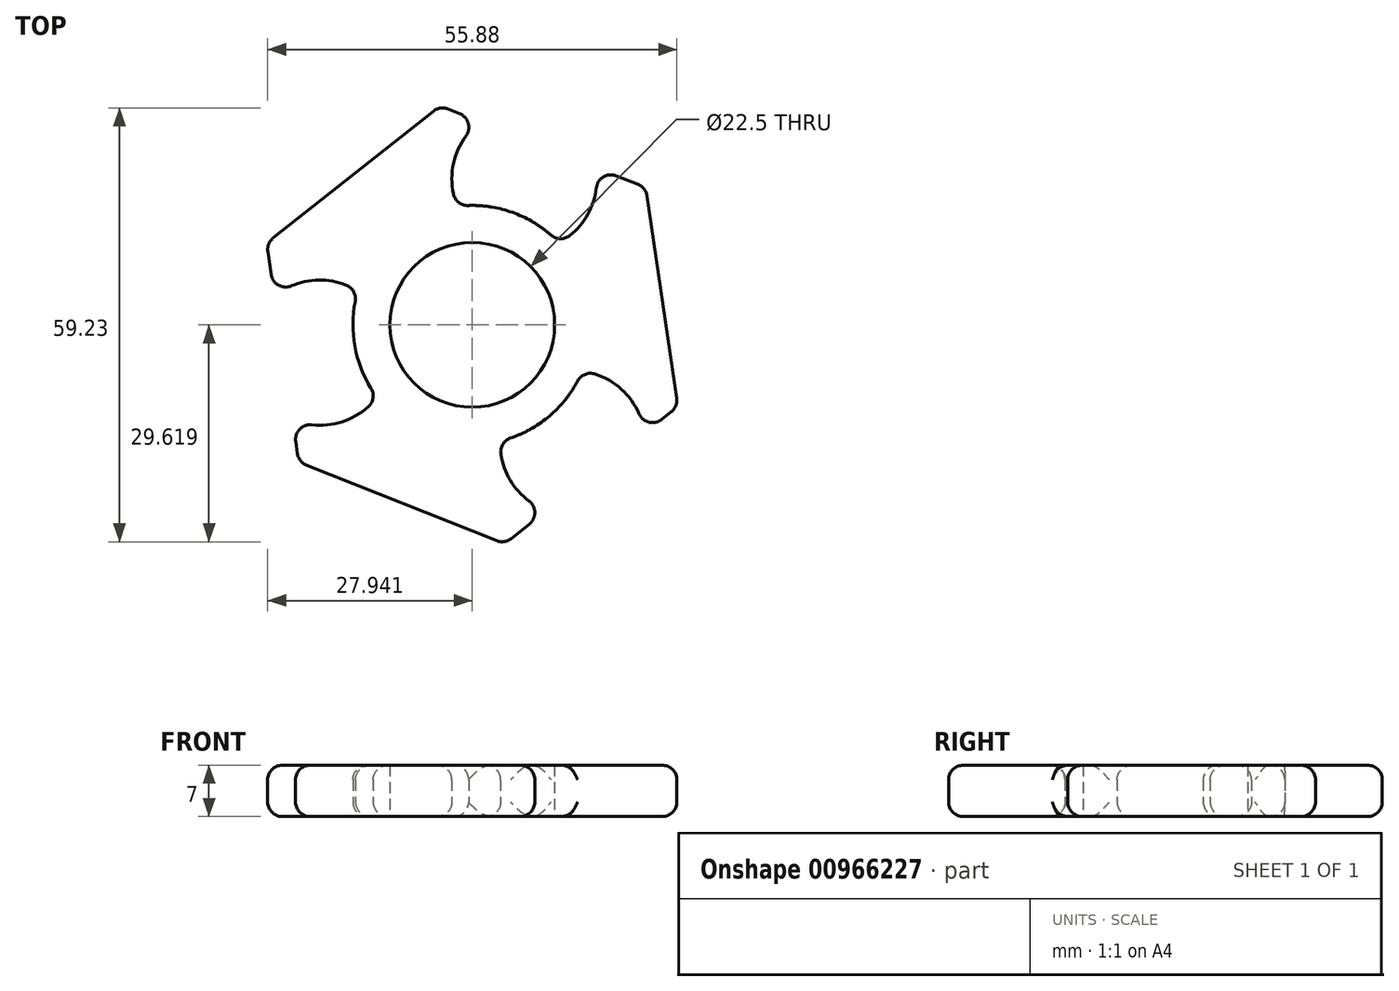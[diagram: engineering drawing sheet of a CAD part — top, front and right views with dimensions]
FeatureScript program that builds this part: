
annotation { "Feature Type Name" : "Feature", "Feature Type Description" : "" }
export const myFeature = defineFeature(function(context is Context, id is Id, definition is map)
    precondition{}
    {
        {
            var Q0;
            Q0=qCreatedBy(makeId("Top.planeOp"),FACE);
            var sketch = newSketch(context, id + "F0", { "sketchPlane" : qUnion([Q0])});
            skCircle(sketch, "E0", {"center": v(-239.75, -46.72) * mm, "radius": 11.25 * mm});
            skCircle(sketch, "E1.cCircle", {"center": v(-239.75, -46.72) * mm, "radius": 26.17 * mm, "construction": true});
            skLineSegment(sketch, "E1.0", {"start": v(-216.05, -27.97) * mm, "end": v(-211.66, -57.87) * mm});
            skLineSegment(sketch, "E1.1", {"start": v(-211.66, -57.87) * mm, "end": v(-235.36, -76.62) * mm});
            skLineSegment(sketch, "E1.2", {"start": v(-235.36, -76.62) * mm, "end": v(-263.45, -65.47) * mm});
            skLineSegment(sketch, "E1.3", {"start": v(-263.45, -65.47) * mm, "end": v(-267.84, -35.57) * mm});
            skLineSegment(sketch, "E1.4", {"start": v(-267.84, -35.57) * mm, "end": v(-244.14, -16.82) * mm});
            skLineSegment(sketch, "E1.5", {"start": v(-244.14, -16.82) * mm, "end": v(-216.05, -27.97) * mm});
            skPoint(sketch, "E1.0.midPoint", {"position": v(-213.85, -42.92) * mm});
            skCircle(sketch, "E2", {"center": v(-260.57, -50.52) * mm, "radius": 9.91 * mm});
            skPoint(sketch, "E2.centerSnap0", {"position": v(-265.64, -50.52) * mm});
            skCircle(sketch, "E3.1.0", {"center": v(-226.05, -62.85) * mm, "radius": 9.91 * mm});
            skCircle(sketch, "E3.2.0", {"center": v(-232.63, -26.8) * mm, "radius": 9.91 * mm});
            skCircle(sketch, "E4", {"center": v(-239.75, -46.72) * mm, "radius": 16.3 * mm});
            skSolve(sketch);
        }
        {
            var Q0;
            {var subQ1=sQuery(id+"F0.wireOp",EDGE,"E1.0");Q0=makeQuery(id+"F0.imprint","IMPRINT",FACE,{"disambiguationData":[TD([[makeQuery(id+"F0.imprint","IMPRINT",EDGE,{"derivedFrom":subQ1}),-1.0]])]});}
            var Q1;
            {var subQ1=sQuery(id+"F0.wireOp",EDGE,"E1.4");Q1=makeQuery(id+"F0.imprint","IMPRINT",FACE,{"disambiguationData":[TD([[makeQuery(id+"F0.imprint","IMPRINT",EDGE,{"derivedFrom":subQ1}),-1.0]])]});}
            var Q2;
            {var subQ1=sQuery(id+"F0.wireOp",EDGE,"E1.2");Q2=makeQuery(id+"F0.imprint","IMPRINT",FACE,{"disambiguationData":[TD([[makeQuery(id+"F0.imprint","IMPRINT",EDGE,{"derivedFrom":subQ1}),-1.0]])]});}
            var Q3;
            {var subQ0=sQuery(id+"F0.wireOp",EDGE,"E2");var subQ1=sQuery(id+"F0.wireOp",EDGE,"E0");var subQ2=makeQuery(id+"F0.imprint","INTERSECT",VERTEX,{"derivedFrom":[subQ1,subQ0]});Q3=makeQuery(id+"F0.imprint","IMPRINT",FACE,{"disambiguationData":[TD([[makeQuery(id+"F0.imprint","IMPRINT",EDGE,{"disambiguationData":[TD([[subQ2,1.0]])],"derivedFrom":subQ1}),-1.0]])]});}
            var Q4;
            {var subQ0=sQuery(id+"F0.wireOp",EDGE,"E2");var subQ1=makeQuery(id+"F0.imprint","INTERSECT",VERTEX,{"derivedFrom":[sQuery(id+"F0.wireOp",EDGE,"E0"),subQ0]});Q4=makeQuery(id+"F0.imprint","IMPRINT",FACE,{"disambiguationData":[TD([[makeQuery(id+"F0.imprint","IMPRINT",EDGE,{"disambiguationData":[TD([[subQ1,-1.0]])],"derivedFrom":subQ0}),1.0]])]});}
            var Q5;
            {var subQ0=sQuery(id+"F0.wireOp",EDGE,"E2");var subQ1=sQuery(id+"F0.wireOp",EDGE,"E0");var subQ2=makeQuery(id+"F0.imprint","INTERSECT",VERTEX,{"derivedFrom":[subQ1,subQ0]});Q5=makeQuery(id+"F0.imprint","IMPRINT",FACE,{"disambiguationData":[TD([[makeQuery(id+"F0.imprint","IMPRINT",EDGE,{"disambiguationData":[TD([[subQ2,-1.0]])],"derivedFrom":subQ1}),-1.0]])]});}
            var Q6;
            {var subQ0=sQuery(id+"F0.wireOp",EDGE,"E3.1.0");var subQ1=makeQuery(id+"F0.imprint","INTERSECT",VERTEX,{"derivedFrom":[sQuery(id+"F0.wireOp",EDGE,"E0"),subQ0]});Q6=makeQuery(id+"F0.imprint","IMPRINT",FACE,{"disambiguationData":[TD([[makeQuery(id+"F0.imprint","IMPRINT",EDGE,{"disambiguationData":[TD([[subQ1,-1.0]])],"derivedFrom":subQ0}),1.0]])]});}
            var Q7;
            {var subQ0=sQuery(id+"F0.wireOp",EDGE,"E3.2.0");var subQ1=sQuery(id+"F0.wireOp",EDGE,"E0");var subQ2=makeQuery(id+"F0.imprint","INTERSECT",VERTEX,{"derivedFrom":[subQ1,subQ0]});Q7=makeQuery(id+"F0.imprint","IMPRINT",FACE,{"disambiguationData":[TD([[makeQuery(id+"F0.imprint","IMPRINT",EDGE,{"disambiguationData":[TD([[subQ2,1.0]])],"derivedFrom":subQ1}),-1.0]])]});}
            var Q8;
            {var subQ0=sQuery(id+"F0.wireOp",EDGE,"E3.2.0");var subQ1=makeQuery(id+"F0.imprint","INTERSECT",VERTEX,{"derivedFrom":[sQuery(id+"F0.wireOp",EDGE,"E0"),subQ0]});Q8=makeQuery(id+"F0.imprint","IMPRINT",FACE,{"disambiguationData":[TD([[makeQuery(id+"F0.imprint","IMPRINT",EDGE,{"disambiguationData":[TD([[subQ1,-1.0]])],"derivedFrom":subQ0}),1.0]])]});}
            extrude(context, id + "F1", {"entities" : qUnion([Q0, Q1, Q2, Q3, Q4, Q5, Q6, Q7, Q8]), "depth" : 7 * mm, "offsetDistance" : 25 * mm});
        }
        {
            var Q0;
            Q0=makeQuery(id+"F1.opExtrude","CAP_EDGE",EDGE,{"disambiguationData":[OSD([sQuery(id+"F0.wireOp",EDGE,"E1.4")])],"isStart":false});
            var Q1;
            Q1=makeQuery(id+"F1.opExtrude","CAP_EDGE",EDGE,{"disambiguationData":[OSD([sQuery(id+"F0.wireOp",EDGE,"E1.0")])],"isStart":false});
            var Q2;
            Q2=makeQuery(id+"F1.opExtrude","CAP_EDGE",EDGE,{"disambiguationData":[OSD([sQuery(id+"F0.wireOp",EDGE,"E1.2")])],"isStart":false});
            var Q3;
            {var subQ0=sQuery(id+"F0.wireOp",EDGE,"E1.3");Q3=makeQuery(id+"F1.opExtrude","CAP_EDGE",EDGE,{"disambiguationData":[OSD([subQ0]),TDD([makeQuery(id+"F0.imprint","IMPRINT",EDGE,{"disambiguationData":[TD([[makeQuery(id+"F0.imprint","INTERSECT",VERTEX,{"derivedFrom":[subQ0,sQuery(id+"F0.wireOp",EDGE,"E1.4")]}),1.0]])],"derivedFrom":subQ0})])],"isStart":false});}
            var Q4;
            {var subQ0=sQuery(id+"F0.wireOp",EDGE,"E1.3");Q4=makeQuery(id+"F1.opExtrude","CAP_EDGE",EDGE,{"disambiguationData":[OSD([subQ0]),TDD([makeQuery(id+"F0.imprint","IMPRINT",EDGE,{"disambiguationData":[TD([[makeQuery(id+"F0.imprint","INTERSECT",VERTEX,{"derivedFrom":[sQuery(id+"F0.wireOp",EDGE,"E1.2"),subQ0]}),-1.0]])],"derivedFrom":subQ0})])],"isStart":false});}
            var Q5;
            {var subQ0=sQuery(id+"F0.wireOp",EDGE,"E4");var subQ1=sQuery(id+"F0.wireOp",EDGE,"E2");Q5=makeQuery(id+"F1.opExtrude","CAP_EDGE",EDGE,{"disambiguationData":[OSD([subQ0]),TDD([makeQuery(id+"F0.imprint","IMPRINT",EDGE,{"disambiguationData":[TD([[makeQuery(id+"F0.imprint","INTERSECT",VERTEX,{"disambiguationData":[OD(0.0)],"derivedFrom":[subQ1,subQ0]}),-1.0]])],"derivedFrom":subQ0})])],"isStart":false});}
            var Q6;
            {var subQ0=sQuery(id+"F0.wireOp",EDGE,"E2");Q6=makeQuery(id+"F1.opExtrude","CAP_EDGE",EDGE,{"disambiguationData":[OSD([subQ0]),TDD([makeQuery(id+"F0.imprint","IMPRINT",EDGE,{"disambiguationData":[TD([[makeQuery(id+"F0.imprint","INTERSECT",VERTEX,{"disambiguationData":[OD(1.0)],"derivedFrom":[sQuery(id+"F0.wireOp",EDGE,"E1.3"),subQ0]}),1.0]])],"derivedFrom":subQ0})])],"isStart":false});}
            var Q7;
            {var subQ0=sQuery(id+"F0.wireOp",EDGE,"E2");Q7=makeQuery(id+"F1.opExtrude","CAP_EDGE",EDGE,{"disambiguationData":[OSD([subQ0]),TDD([makeQuery(id+"F0.imprint","IMPRINT",EDGE,{"disambiguationData":[TD([[makeQuery(id+"F0.imprint","INTERSECT",VERTEX,{"disambiguationData":[OD(0.0)],"derivedFrom":[sQuery(id+"F0.wireOp",EDGE,"E1.3"),subQ0]}),-1.0]])],"derivedFrom":subQ0})])],"isStart":false});}
            var Q8;
            {var subQ0=sQuery(id+"F0.wireOp",EDGE,"E3.1.0");Q8=makeQuery(id+"F1.opExtrude","CAP_EDGE",EDGE,{"disambiguationData":[OSD([subQ0]),TDD([makeQuery(id+"F0.imprint","IMPRINT",EDGE,{"disambiguationData":[TD([[makeQuery(id+"F0.imprint","INTERSECT",VERTEX,{"disambiguationData":[OD(1.0)],"derivedFrom":[sQuery(id+"F0.wireOp",EDGE,"E1.1"),subQ0]}),1.0]])],"derivedFrom":subQ0})])],"isStart":false});}
            var Q9;
            {var subQ0=sQuery(id+"F0.wireOp",EDGE,"E4");var subQ1=sQuery(id+"F0.wireOp",EDGE,"E3.1.0");Q9=makeQuery(id+"F1.opExtrude","SWEPT_FACE",FACE,{"disambiguationData":[OSD([subQ0]),TDD([makeQuery(id+"F0.imprint","IMPRINT",EDGE,{"disambiguationData":[TD([[makeQuery(id+"F0.imprint","INTERSECT",VERTEX,{"disambiguationData":[OD(0.0)],"derivedFrom":[subQ1,subQ0]}),-1.0]])],"derivedFrom":subQ0})])]});}
            var Q10;
            {var subQ0=sQuery(id+"F0.wireOp",EDGE,"E2");Q10=makeQuery(id+"F1.opExtrude","CAP_EDGE",EDGE,{"disambiguationData":[OSD([subQ0]),TDD([makeQuery(id+"F0.imprint","IMPRINT",EDGE,{"disambiguationData":[TD([[makeQuery(id+"F0.imprint","INTERSECT",VERTEX,{"disambiguationData":[OD(1.0)],"derivedFrom":[sQuery(id+"F0.wireOp",EDGE,"E1.3"),subQ0]}),1.0]])],"derivedFrom":subQ0})])],"isStart":true});}
            var Q11;
            {var subQ0=sQuery(id+"F0.wireOp",EDGE,"E4");var subQ1=sQuery(id+"F0.wireOp",EDGE,"E3.2.0");Q11=makeQuery(id+"F1.opExtrude","CAP_EDGE",EDGE,{"disambiguationData":[OSD([subQ0]),TDD([makeQuery(id+"F0.imprint","IMPRINT",EDGE,{"disambiguationData":[TD([[makeQuery(id+"F0.imprint","INTERSECT",VERTEX,{"disambiguationData":[OD(0.0)],"derivedFrom":[subQ1,subQ0]}),-1.0]])],"derivedFrom":subQ0})])],"isStart":false});}
            var Q12;
            {var subQ0=sQuery(id+"F0.wireOp",EDGE,"E4");var subQ1=sQuery(id+"F0.wireOp",EDGE,"E3.2.0");Q12=makeQuery(id+"F1.opExtrude","CAP_EDGE",EDGE,{"disambiguationData":[OSD([subQ0]),TDD([makeQuery(id+"F0.imprint","IMPRINT",EDGE,{"disambiguationData":[TD([[makeQuery(id+"F0.imprint","INTERSECT",VERTEX,{"disambiguationData":[OD(0.0)],"derivedFrom":[subQ1,subQ0]}),-1.0]])],"derivedFrom":subQ0})])],"isStart":true});}
            var Q13;
            {var subQ0=sQuery(id+"F0.wireOp",EDGE,"E3.1.0");Q13=makeQuery(id+"F1.opExtrude","CAP_EDGE",EDGE,{"disambiguationData":[OSD([subQ0]),TDD([makeQuery(id+"F0.imprint","IMPRINT",EDGE,{"disambiguationData":[TD([[makeQuery(id+"F0.imprint","INTERSECT",VERTEX,{"disambiguationData":[OD(1.0)],"derivedFrom":[sQuery(id+"F0.wireOp",EDGE,"E1.1"),subQ0]}),1.0]])],"derivedFrom":subQ0})])],"isStart":true});}
            var Q14;
            Q14=makeQuery(id+"F1.opExtrude","SWEPT_EDGE",EDGE,{"disambiguationData":[OSD([sQuery(id+"F0.wireOp",EDGE,"E1.4"),sQuery(id+"F0.wireOp",EDGE,"E1.5")])]});
            var Q15;
            Q15=makeQuery(id+"F1.opExtrude","SWEPT_EDGE",EDGE,{"disambiguationData":[OSD([sQuery(id+"F0.wireOp",EDGE,"E1.0"),sQuery(id+"F0.wireOp",EDGE,"E1.5")])]});
            var Q16;
            {var subQ0=sQuery(id+"F0.wireOp",EDGE,"E3.1.0");Q16=makeQuery(id+"F1.opExtrude","CAP_EDGE",EDGE,{"disambiguationData":[OSD([subQ0]),TDD([makeQuery(id+"F0.imprint","IMPRINT",EDGE,{"disambiguationData":[TD([[makeQuery(id+"F0.imprint","INTERSECT",VERTEX,{"disambiguationData":[OD(0.0)],"derivedFrom":[sQuery(id+"F0.wireOp",EDGE,"E1.1"),subQ0]}),-1.0]])],"derivedFrom":subQ0})])],"isStart":true});}
            var Q17;
            {var subQ0=sQuery(id+"F0.wireOp",EDGE,"E1.1");Q17=makeQuery(id+"F1.opExtrude","CAP_EDGE",EDGE,{"disambiguationData":[OSD([subQ0]),TDD([makeQuery(id+"F0.imprint","IMPRINT",EDGE,{"disambiguationData":[TD([[makeQuery(id+"F0.imprint","INTERSECT",VERTEX,{"derivedFrom":[sQuery(id+"F0.wireOp",EDGE,"E1.0"),subQ0]}),-1.0]])],"derivedFrom":subQ0})])],"isStart":true});}
            var Q18;
            {var subQ0=sQuery(id+"F0.wireOp",EDGE,"E4");var subQ1=sQuery(id+"F0.wireOp",EDGE,"E2");Q18=makeQuery(id+"F1.opExtrude","CAP_EDGE",EDGE,{"disambiguationData":[OSD([subQ0]),TDD([makeQuery(id+"F0.imprint","IMPRINT",EDGE,{"disambiguationData":[TD([[makeQuery(id+"F0.imprint","INTERSECT",VERTEX,{"disambiguationData":[OD(0.0)],"derivedFrom":[subQ1,subQ0]}),-1.0]])],"derivedFrom":subQ0})])],"isStart":true});}
            var Q19;
            {var subQ0=sQuery(id+"F0.wireOp",EDGE,"E4");var subQ1=sQuery(id+"F0.wireOp",EDGE,"E3.1.0");Q19=makeQuery(id+"F1.opExtrude","CAP_EDGE",EDGE,{"disambiguationData":[OSD([subQ0]),TDD([makeQuery(id+"F0.imprint","IMPRINT",EDGE,{"disambiguationData":[TD([[makeQuery(id+"F0.imprint","INTERSECT",VERTEX,{"disambiguationData":[OD(0.0)],"derivedFrom":[subQ1,subQ0]}),-1.0]])],"derivedFrom":subQ0})])],"isStart":true});}
            var Q20;
            Q20=makeQuery(id+"F1.opExtrude","SWEPT_EDGE",EDGE,{"disambiguationData":[OSD([sQuery(id+"F0.wireOp",EDGE,"E1.0"),sQuery(id+"F0.wireOp",EDGE,"E1.1")])]});
            var Q21;
            Q21=makeQuery(id+"F1.opExtrude","SWEPT_EDGE",EDGE,{"disambiguationData":[OSD([sQuery(id+"F0.wireOp",EDGE,"E1.3"),sQuery(id+"F0.wireOp",EDGE,"E1.4")])]});
            var Q22;
            Q22=makeQuery(id+"F1.opExtrude","SWEPT_EDGE",EDGE,{"disambiguationData":[OSD([sQuery(id+"F0.wireOp",EDGE,"E1.2"),sQuery(id+"F0.wireOp",EDGE,"E1.3")])]});
            var Q23;
            {var subQ0=sQuery(id+"F0.wireOp",EDGE,"E4");var subQ1=sQuery(id+"F0.wireOp",EDGE,"E2");Q23=makeQuery(id+"F1.opExtrude","SWEPT_EDGE",EDGE,{"disambiguationData":[OSD([subQ1,subQ0]),TDD([makeQuery(id+"F0.imprint","INTERSECT",VERTEX,{"disambiguationData":[OD(1.0)],"derivedFrom":[subQ1,subQ0]})])]});}
            var Q24;
            {var subQ0=sQuery(id+"F0.wireOp",EDGE,"E1.1");Q24=makeQuery(id+"F1.opExtrude","CAP_EDGE",EDGE,{"disambiguationData":[OSD([subQ0]),TDD([makeQuery(id+"F0.imprint","IMPRINT",EDGE,{"disambiguationData":[TD([[makeQuery(id+"F0.imprint","INTERSECT",VERTEX,{"derivedFrom":[sQuery(id+"F0.wireOp",EDGE,"E1.0"),subQ0]}),-1.0]])],"derivedFrom":subQ0})])],"isStart":false});}
            var Q25;
            Q25=makeQuery(id+"F1.opExtrude","CAP_EDGE",EDGE,{"disambiguationData":[OSD([sQuery(id+"F0.wireOp",EDGE,"E1.4")])],"isStart":true});
            var Q26;
            {var subQ0=sQuery(id+"F0.wireOp",EDGE,"E3.1.0");Q26=makeQuery(id+"F1.opExtrude","CAP_EDGE",EDGE,{"disambiguationData":[OSD([subQ0]),TDD([makeQuery(id+"F0.imprint","IMPRINT",EDGE,{"disambiguationData":[TD([[makeQuery(id+"F0.imprint","INTERSECT",VERTEX,{"disambiguationData":[OD(0.0)],"derivedFrom":[sQuery(id+"F0.wireOp",EDGE,"E1.1"),subQ0]}),-1.0]])],"derivedFrom":subQ0})])],"isStart":false});}
            var Q27;
            Q27=makeQuery(id+"F1.opExtrude","SWEPT_EDGE",EDGE,{"disambiguationData":[OSD([sQuery(id+"F0.wireOp",EDGE,"E1.1"),sQuery(id+"F0.wireOp",EDGE,"E1.2")])]});
            var Q28;
            {var subQ0=sQuery(id+"F0.wireOp",EDGE,"E4");var subQ1=sQuery(id+"F0.wireOp",EDGE,"E3.1.0");Q28=makeQuery(id+"F1.opExtrude","SWEPT_EDGE",EDGE,{"disambiguationData":[OSD([subQ1,subQ0]),TDD([makeQuery(id+"F0.imprint","INTERSECT",VERTEX,{"disambiguationData":[OD(1.0)],"derivedFrom":[subQ1,subQ0]})])]});}
            var Q29;
            {var subQ0=sQuery(id+"F0.wireOp",EDGE,"E1.3");Q29=makeQuery(id+"F1.opExtrude","CAP_EDGE",EDGE,{"disambiguationData":[OSD([subQ0]),TDD([makeQuery(id+"F0.imprint","IMPRINT",EDGE,{"disambiguationData":[TD([[makeQuery(id+"F0.imprint","INTERSECT",VERTEX,{"derivedFrom":[subQ0,sQuery(id+"F0.wireOp",EDGE,"E1.4")]}),1.0]])],"derivedFrom":subQ0})])],"isStart":true});}
            var Q30;
            {var subQ0=sQuery(id+"F0.wireOp",EDGE,"E2");var subQ1=sQuery(id+"F0.wireOp",EDGE,"E1.3");Q30=makeQuery(id+"F1.opExtrude","SWEPT_EDGE",EDGE,{"disambiguationData":[OSD([subQ1,subQ0]),TDD([makeQuery(id+"F0.imprint","INTERSECT",VERTEX,{"disambiguationData":[OD(1.0)],"derivedFrom":[subQ1,subQ0]})])]});}
            var Q31;
            {var subQ0=sQuery(id+"F0.wireOp",EDGE,"E4");var subQ1=sQuery(id+"F0.wireOp",EDGE,"E3.1.0");Q31=makeQuery(id+"F1.opExtrude","SWEPT_EDGE",EDGE,{"disambiguationData":[OSD([subQ1,subQ0]),TDD([makeQuery(id+"F0.imprint","INTERSECT",VERTEX,{"disambiguationData":[OD(0.0)],"derivedFrom":[subQ1,subQ0]})])]});}
            var Q32;
            {var subQ0=sQuery(id+"F0.wireOp",EDGE,"E3.2.0");Q32=makeQuery(id+"F1.opExtrude","CAP_EDGE",EDGE,{"disambiguationData":[OSD([subQ0]),TDD([makeQuery(id+"F0.imprint","IMPRINT",EDGE,{"disambiguationData":[TD([[makeQuery(id+"F0.imprint","INTERSECT",VERTEX,{"disambiguationData":[OD(0.0)],"derivedFrom":[sQuery(id+"F0.wireOp",EDGE,"E1.5"),subQ0]}),-1.0]])],"derivedFrom":subQ0})])],"isStart":false});}
            var Q33;
            {var subQ0=sQuery(id+"F0.wireOp",EDGE,"E3.2.0");Q33=makeQuery(id+"F1.opExtrude","CAP_EDGE",EDGE,{"disambiguationData":[OSD([subQ0]),TDD([makeQuery(id+"F0.imprint","IMPRINT",EDGE,{"disambiguationData":[TD([[makeQuery(id+"F0.imprint","INTERSECT",VERTEX,{"disambiguationData":[OD(0.0)],"derivedFrom":[sQuery(id+"F0.wireOp",EDGE,"E1.5"),subQ0]}),-1.0]])],"derivedFrom":subQ0})])],"isStart":true});}
            var Q34;
            {var subQ0=sQuery(id+"F0.wireOp",EDGE,"E3.1.0");var subQ1=sQuery(id+"F0.wireOp",EDGE,"E1.1");Q34=makeQuery(id+"F1.opExtrude","SWEPT_EDGE",EDGE,{"disambiguationData":[OSD([subQ1,subQ0]),TDD([makeQuery(id+"F0.imprint","INTERSECT",VERTEX,{"disambiguationData":[OD(1.0)],"derivedFrom":[subQ1,subQ0]})])]});}
            var Q35;
            {var subQ0=sQuery(id+"F0.wireOp",EDGE,"E3.2.0");var subQ1=sQuery(id+"F0.wireOp",EDGE,"E1.5");Q35=makeQuery(id+"F1.opExtrude","SWEPT_EDGE",EDGE,{"disambiguationData":[OSD([subQ1,subQ0]),TDD([makeQuery(id+"F0.imprint","INTERSECT",VERTEX,{"disambiguationData":[OD(1.0)],"derivedFrom":[subQ1,subQ0]})])]});}
            var Q36;
            {var subQ0=sQuery(id+"F0.wireOp",EDGE,"E1.5");Q36=makeQuery(id+"F1.opExtrude","CAP_EDGE",EDGE,{"disambiguationData":[OSD([subQ0]),TDD([makeQuery(id+"F0.imprint","IMPRINT",EDGE,{"disambiguationData":[TD([[makeQuery(id+"F0.imprint","INTERSECT",VERTEX,{"derivedFrom":[sQuery(id+"F0.wireOp",EDGE,"E1.0"),subQ0]}),1.0]])],"derivedFrom":subQ0})])],"isStart":false});}
            var Q37;
            Q37=makeQuery(id+"F1.opExtrude","CAP_EDGE",EDGE,{"disambiguationData":[OSD([sQuery(id+"F0.wireOp",EDGE,"E1.0")])],"isStart":true});
            var Q38;
            {var subQ0=sQuery(id+"F0.wireOp",EDGE,"E4");var subQ1=sQuery(id+"F0.wireOp",EDGE,"E3.2.0");Q38=makeQuery(id+"F1.opExtrude","SWEPT_EDGE",EDGE,{"disambiguationData":[OSD([subQ1,subQ0]),TDD([makeQuery(id+"F0.imprint","INTERSECT",VERTEX,{"disambiguationData":[OD(1.0)],"derivedFrom":[subQ1,subQ0]})])]});}
            var Q39;
            {var subQ0=sQuery(id+"F0.wireOp",EDGE,"E3.2.0");Q39=makeQuery(id+"F1.opExtrude","CAP_EDGE",EDGE,{"disambiguationData":[OSD([subQ0]),TDD([makeQuery(id+"F0.imprint","IMPRINT",EDGE,{"disambiguationData":[TD([[makeQuery(id+"F0.imprint","INTERSECT",VERTEX,{"disambiguationData":[OD(1.0)],"derivedFrom":[sQuery(id+"F0.wireOp",EDGE,"E1.5"),subQ0]}),1.0]])],"derivedFrom":subQ0})])],"isStart":true});}
            var Q40;
            {var subQ0=sQuery(id+"F0.wireOp",EDGE,"E4");var subQ1=sQuery(id+"F0.wireOp",EDGE,"E3.1.0");Q40=makeQuery(id+"F1.opExtrude","CAP_EDGE",EDGE,{"disambiguationData":[OSD([subQ0]),TDD([makeQuery(id+"F0.imprint","IMPRINT",EDGE,{"disambiguationData":[TD([[makeQuery(id+"F0.imprint","INTERSECT",VERTEX,{"disambiguationData":[OD(0.0)],"derivedFrom":[subQ1,subQ0]}),-1.0]])],"derivedFrom":subQ0})])],"isStart":false});}
            var Q41;
            {var subQ0=sQuery(id+"F0.wireOp",EDGE,"E1.3");Q41=makeQuery(id+"F1.opExtrude","CAP_EDGE",EDGE,{"disambiguationData":[OSD([subQ0]),TDD([makeQuery(id+"F0.imprint","IMPRINT",EDGE,{"disambiguationData":[TD([[makeQuery(id+"F0.imprint","INTERSECT",VERTEX,{"derivedFrom":[sQuery(id+"F0.wireOp",EDGE,"E1.2"),subQ0]}),-1.0]])],"derivedFrom":subQ0})])],"isStart":true});}
            var Q42;
            {var subQ0=sQuery(id+"F0.wireOp",EDGE,"E1.5");Q42=makeQuery(id+"F1.opExtrude","CAP_EDGE",EDGE,{"disambiguationData":[OSD([subQ0]),TDD([makeQuery(id+"F0.imprint","IMPRINT",EDGE,{"disambiguationData":[TD([[makeQuery(id+"F0.imprint","INTERSECT",VERTEX,{"derivedFrom":[sQuery(id+"F0.wireOp",EDGE,"E1.4"),subQ0]}),-1.0]])],"derivedFrom":subQ0})])],"isStart":true});}
            var Q43;
            {var subQ0=sQuery(id+"F0.wireOp",EDGE,"E1.5");Q43=makeQuery(id+"F1.opExtrude","CAP_EDGE",EDGE,{"disambiguationData":[OSD([subQ0]),TDD([makeQuery(id+"F0.imprint","IMPRINT",EDGE,{"disambiguationData":[TD([[makeQuery(id+"F0.imprint","INTERSECT",VERTEX,{"derivedFrom":[sQuery(id+"F0.wireOp",EDGE,"E1.0"),subQ0]}),1.0]])],"derivedFrom":subQ0})])],"isStart":true});}
            var Q44;
            {var subQ0=sQuery(id+"F0.wireOp",EDGE,"E3.2.0");var subQ1=sQuery(id+"F0.wireOp",EDGE,"E1.5");Q44=makeQuery(id+"F1.opExtrude","SWEPT_EDGE",EDGE,{"disambiguationData":[OSD([subQ1,subQ0]),TDD([makeQuery(id+"F0.imprint","INTERSECT",VERTEX,{"disambiguationData":[OD(0.0)],"derivedFrom":[subQ1,subQ0]})])]});}
            var Q45;
            {var subQ0=sQuery(id+"F0.wireOp",EDGE,"E1.1");Q45=makeQuery(id+"F1.opExtrude","CAP_EDGE",EDGE,{"disambiguationData":[OSD([subQ0]),TDD([makeQuery(id+"F0.imprint","IMPRINT",EDGE,{"disambiguationData":[TD([[makeQuery(id+"F0.imprint","INTERSECT",VERTEX,{"derivedFrom":[subQ0,sQuery(id+"F0.wireOp",EDGE,"E1.2")]}),1.0]])],"derivedFrom":subQ0})])],"isStart":true});}
            var Q46;
            {var subQ0=sQuery(id+"F0.wireOp",EDGE,"E2");Q46=makeQuery(id+"F1.opExtrude","CAP_EDGE",EDGE,{"disambiguationData":[OSD([subQ0]),TDD([makeQuery(id+"F0.imprint","IMPRINT",EDGE,{"disambiguationData":[TD([[makeQuery(id+"F0.imprint","INTERSECT",VERTEX,{"disambiguationData":[OD(0.0)],"derivedFrom":[sQuery(id+"F0.wireOp",EDGE,"E1.3"),subQ0]}),-1.0]])],"derivedFrom":subQ0})])],"isStart":true});}
            var Q47;
            {var subQ0=sQuery(id+"F0.wireOp",EDGE,"E4");var subQ1=sQuery(id+"F0.wireOp",EDGE,"E3.2.0");Q47=makeQuery(id+"F1.opExtrude","SWEPT_EDGE",EDGE,{"disambiguationData":[OSD([subQ1,subQ0]),TDD([makeQuery(id+"F0.imprint","INTERSECT",VERTEX,{"disambiguationData":[OD(0.0)],"derivedFrom":[subQ1,subQ0]})])]});}
            var Q48;
            {var subQ0=sQuery(id+"F0.wireOp",EDGE,"E3.1.0");var subQ1=sQuery(id+"F0.wireOp",EDGE,"E1.1");Q48=makeQuery(id+"F1.opExtrude","SWEPT_EDGE",EDGE,{"disambiguationData":[OSD([subQ1,subQ0]),TDD([makeQuery(id+"F0.imprint","INTERSECT",VERTEX,{"disambiguationData":[OD(0.0)],"derivedFrom":[subQ1,subQ0]})])]});}
            var Q49;
            {var subQ0=sQuery(id+"F0.wireOp",EDGE,"E2");var subQ1=sQuery(id+"F0.wireOp",EDGE,"E1.3");Q49=makeQuery(id+"F1.opExtrude","SWEPT_EDGE",EDGE,{"disambiguationData":[OSD([subQ1,subQ0]),TDD([makeQuery(id+"F0.imprint","INTERSECT",VERTEX,{"disambiguationData":[OD(0.0)],"derivedFrom":[subQ1,subQ0]})])]});}
            var Q50;
            {var subQ0=sQuery(id+"F0.wireOp",EDGE,"E3.2.0");Q50=makeQuery(id+"F1.opExtrude","CAP_EDGE",EDGE,{"disambiguationData":[OSD([subQ0]),TDD([makeQuery(id+"F0.imprint","IMPRINT",EDGE,{"disambiguationData":[TD([[makeQuery(id+"F0.imprint","INTERSECT",VERTEX,{"disambiguationData":[OD(1.0)],"derivedFrom":[sQuery(id+"F0.wireOp",EDGE,"E1.5"),subQ0]}),1.0]])],"derivedFrom":subQ0})])],"isStart":false});}
            var Q51;
            {var subQ0=sQuery(id+"F0.wireOp",EDGE,"E1.5");Q51=makeQuery(id+"F1.opExtrude","CAP_EDGE",EDGE,{"disambiguationData":[OSD([subQ0]),TDD([makeQuery(id+"F0.imprint","IMPRINT",EDGE,{"disambiguationData":[TD([[makeQuery(id+"F0.imprint","INTERSECT",VERTEX,{"derivedFrom":[sQuery(id+"F0.wireOp",EDGE,"E1.4"),subQ0]}),-1.0]])],"derivedFrom":subQ0})])],"isStart":false});}
            var Q52;
            {var subQ0=sQuery(id+"F0.wireOp",EDGE,"E4");var subQ1=sQuery(id+"F0.wireOp",EDGE,"E2");Q52=makeQuery(id+"F1.opExtrude","SWEPT_EDGE",EDGE,{"disambiguationData":[OSD([subQ1,subQ0]),TDD([makeQuery(id+"F0.imprint","INTERSECT",VERTEX,{"disambiguationData":[OD(0.0)],"derivedFrom":[subQ1,subQ0]})])]});}
            var Q53;
            {var subQ0=sQuery(id+"F0.wireOp",EDGE,"E1.1");Q53=makeQuery(id+"F1.opExtrude","CAP_EDGE",EDGE,{"disambiguationData":[OSD([subQ0]),TDD([makeQuery(id+"F0.imprint","IMPRINT",EDGE,{"disambiguationData":[TD([[makeQuery(id+"F0.imprint","INTERSECT",VERTEX,{"derivedFrom":[subQ0,sQuery(id+"F0.wireOp",EDGE,"E1.2")]}),1.0]])],"derivedFrom":subQ0})])],"isStart":false});}
            var Q54;
            Q54=makeQuery(id+"F1.opExtrude","CAP_EDGE",EDGE,{"disambiguationData":[OSD([sQuery(id+"F0.wireOp",EDGE,"E1.2")])],"isStart":true});
            fillet(context, id + "F2", {"entities" : qUnion([Q0, Q1, Q2, Q3, Q4, Q5, Q6, Q7, Q8, Q9, Q10, Q11, Q12, Q13, Q14, Q15, Q16, Q17, Q18, Q19, Q20, Q21, Q22, Q23, Q24, Q25, Q26, Q27, Q28, Q29, Q30, Q31, Q32, Q33, Q34, Q35, Q36, Q37, Q38, Q39, Q40, Q41, Q42, Q43, Q44, Q45, Q46, Q47, Q48, Q49, Q50, Q51, Q52, Q53, Q54]), "radius" : 2 * mm, "tangentPropagation" : true, "allowEdgeOverflow" : false});
        }
    });
